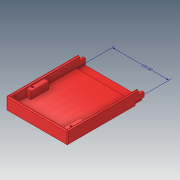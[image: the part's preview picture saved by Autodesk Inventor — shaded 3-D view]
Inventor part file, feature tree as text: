
AUTODESK INVENTOR PART (.ipt)
format: ipt  version: 2019 (Build 230136000, 136)  size: 301,568 bytes
history: native  units: mm
features: sketch x12, extrude x11, projected_geometry x4, other x2, fillet x2, plane x1
ambient origin geometry x8: Origin, YZ Plane, XZ Plane, XY Plane, X Axis, Y Axis, Z Axis, Center Point
bodies: Solid1 (feature_tree)
feature tree (32):
  other  "Annotations"
  extrude  "Extrusion1"  Depth=150.0mm
  extrude  "Extrusion2"  Depth=5.0mm
  extrude  "Extrusion3"  Depth=20.0mm TaperAngle=0.0deg
  extrude  "Extrusion4"  Depth=4.0mm
  fillet  "Fillet1"  Radius=20.0mm
  sketch  "Sketch11"  dims[d23=20.0mm d24=0.0mm d25=2.0mm]
  sketch  "Sketch12"  dims[d37=2.5mm d38=0.0mm d39=35.0mm d40=0.0mm]
  extrude  "Extrusion8"  Depth=2.0mm
  extrude  "Extrusion9"  Depth=35.0mm
  fillet  "Fillet4"  [1 undecoded]
  extrude  "Extrusion10"  Depth=40.0mm
  extrude  "Extrusion11"  TaperAngle=0.0deg  [1 undecoded]
  plane  "Work Plane3"
  extrude  "Extrusion13"  Depth=11.0mm
  extrude  "Extrusion14"  Depth=1.0mm
  extrude  "Extrusion15"  Depth=4.5mm
  sketch  "Sketch1"  dims[d0=135.0mm d1=150.0mm]
  sketch  "Sketch3"  dims[d2=8.0mm d3=0.0mm d4=5.0mm]
  projected_geometry  "Projected Loop2"
  sketch  "Sketch4"  dims[d5=5.0mm d6=20.0mm d7=0.0mm]
  projected_geometry  "Projected Loop3"
  sketch  "Sketch6"  dims[d8=0.0mm d9=4.0mm d10=20.0mm d11=0.0mm]
  sketch  "Sketch15"  dims[d41=10.0mm d42=40.0mm]
  projected_geometry  "Projected Loop7"
  sketch  "Sketch16"  dims[d43=0.0mm d44=0.0mm]
  sketch  "Sketch17"  dims[d45=40.0mm d46=11.0mm]
  sketch  "Sketch21"  dims[d47=16.0mm d48=0.0mm d49=1.0mm]
  sketch  "Sketch22"  dims[d50=4.5mm d51=3.5mm]
  sketch  "Sketch23"  dims[d52=9.0mm d53=4.5mm d54=6.0mm d56=12.0mm d57=0.0mm d60=4.5mm d61=4.5mm d62=30.8mm d64=5.0mm d65=0.0mm d66=0.0mm d67=90.0mm d76=-1.5mm d78=7.5mm d79=7.5mm d80=3.15mm d81=0.0mm d83=10.0mm d85=10.0mm d86=0.0mm d87=13.0mm d88=0.0mm d89=0.0mm d90=12.5mm d91=4.0mm d92=0.0mm d93=4.0mm d94=0.0mm d73=4.870635mm d74=1.41766mm d75=125.0mm]
  projected_geometry  "Projected Loop8"
  other  "Linear Dimension 1"
note: 2 required parameter values undecoded (feature->parameter linkage not recoverable at this tier; creation-order binding heuristic only, values carry confidence <= 0.55)
